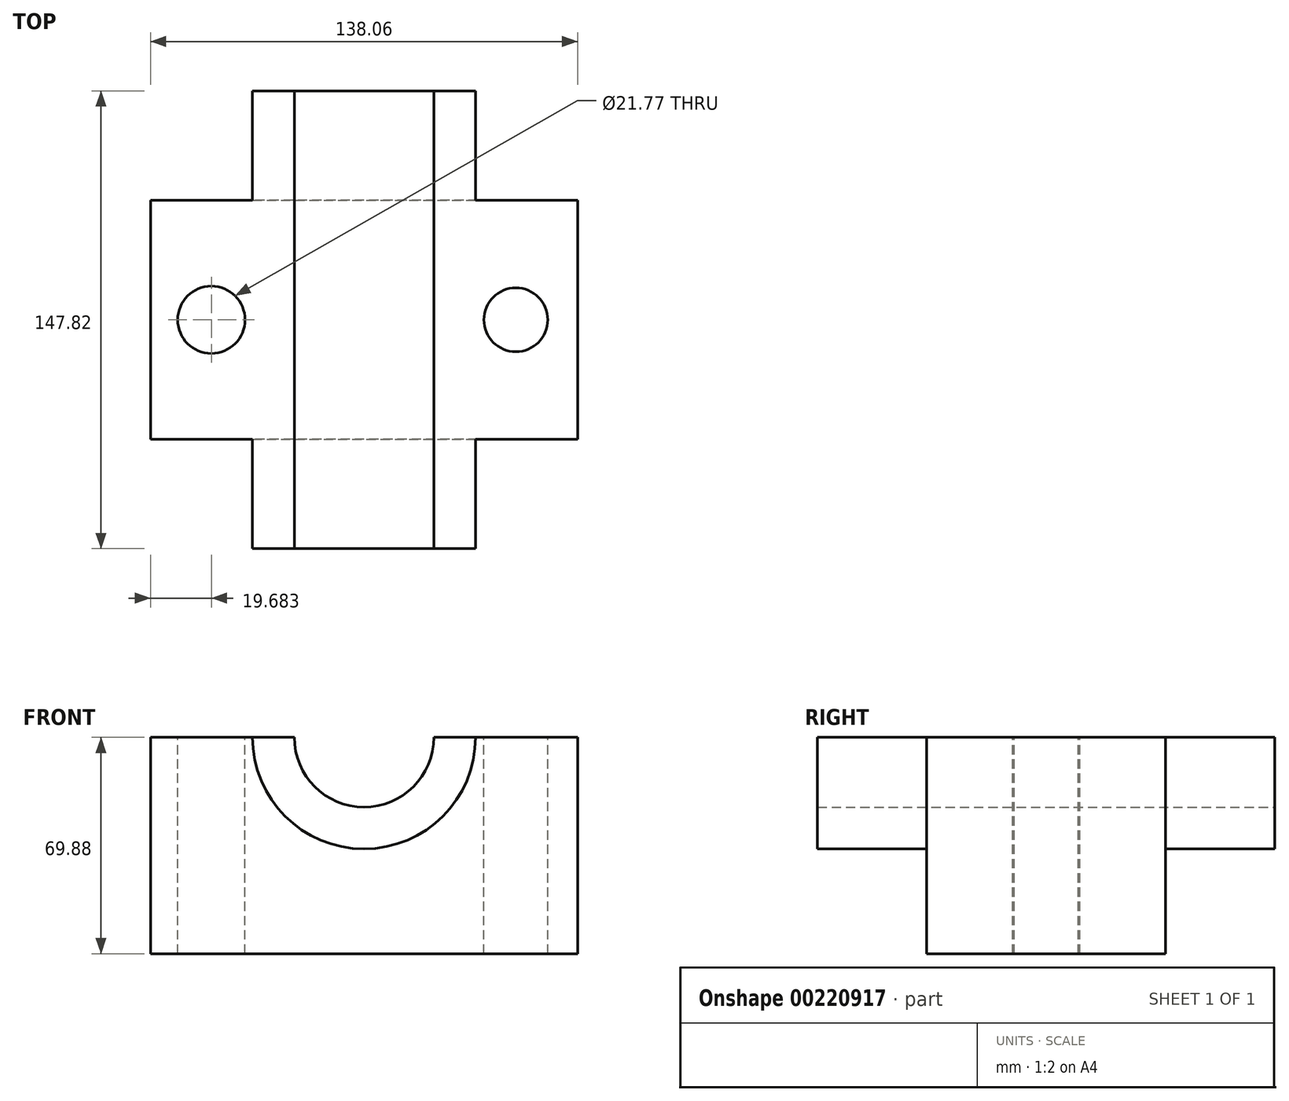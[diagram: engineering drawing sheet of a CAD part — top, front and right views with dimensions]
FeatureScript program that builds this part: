
annotation { "Feature Type Name" : "Feature", "Feature Type Description" : "" }
export const myFeature = defineFeature(function(context is Context, id is Id, definition is map)
    precondition{}
    {
        {
            var Q0;
            Q0=qCreatedBy(makeId("Front.planeOp"),FACE);
            var sketch = newSketch(context, id + "F0", { "sketchPlane" : qUnion([Q0])});
            skLineSegment(sketch, "E0.bottom", {"start": v(69.03, 34.94) * mm, "end": v(-69.03, 34.94) * mm});
            skLineSegment(sketch, "E0.top", {"start": v(69.03, -34.94) * mm, "end": v(-69.03, -34.94) * mm});
            skLineSegment(sketch, "E0.left", {"start": v(69.03, 34.94) * mm, "end": v(69.03, -34.94) * mm});
            skLineSegment(sketch, "E0.right", {"start": v(-69.03, 34.94) * mm, "end": v(-69.03, -34.94) * mm});
            skPoint(sketch, "E0.middle", {"position": v(0, 0) * mm});
            skCircle(sketch, "E1", {"center": v(0, 34.94) * mm, "radius": 36.03 * mm});
            skCircle(sketch, "E2", {"center": v(0, 34.94) * mm, "radius": 22.54 * mm});
            skSolve(sketch);
        }
        {
            var Q0;
            Q0=makeQuery(id+"F0.imprint","IMPRINT",FACE,{"disambiguationData":[TD([[makeQuery(id+"F0.imprint","IMPRINT",EDGE,{"derivedFrom":sQuery(id+"F0.wireOp",EDGE,"E0.bottom")}),1.0]])]});
            extrude(context, id + "F1", {"entities" : qUnion([Q0]), "endBound" : BoundingType.SYMMETRIC, "depth" : 147.83 * mm});
        }
        {
            var Q0;
            Q0 = qSketchRegion(id + "F0", true);
            extrude(context, id + "F2", {"entities" : qUnion([Q0]), "operationType" : NewBodyOperationType.ADD, "endBound" : BoundingType.SYMMETRIC, "oppositeDirection" : true, "depth" : 77.22 * mm});
        }
        {
            var Q0;
            {var subQ0=sQuery(id+"F0.wireOp",EDGE,"E2");var subQ1=sQuery(id+"F0.wireOp",EDGE,"E1");var subQ2=sQuery(id+"F0.wireOp",EDGE,"E0.right");var subQ3=sQuery(id+"F0.wireOp",EDGE,"E0.bottom");var subQ5=sQuery(id+"F0.wireOp",EDGE,"E0.left");var subQ6=makeQuery(id+"F2.opExtrude","CAP_FACE",FACE,{"disambiguationData":[OSD([subQ3,sQuery(id+"F0.wireOp",EDGE,"E0.top"),subQ5,subQ2,subQ1,subQ0])],"isStart":true});Q0=makeQuery(id+"F2.boolean.opBoolean","SPLIT",FACE,{"disambiguationData":[TD([makeQuery(id+"F1.opExtrude","SWEPT_FACE",FACE,{"disambiguationData":[OSD([subQ0])]})])],"derivedFrom":subQ6});}
            extrude(context, id + "F3", {"entities" : qUnion([Q0]), "operationType" : NewBodyOperationType.REMOVE, "oppositeDirection" : true, "depth" : 25.4 * mm});
        }
        {
            var Q0;
            Q0=makeQuery(id+"F3.boolean.opBoolean","COPY",FACE,{"derivedFrom":makeQuery(id+"F3.opExtrude","CAP_FACE",FACE,{"disambiguationData":[OSD([sQuery(id+"F0.wireOp",EDGE,"E0.bottom"),sQuery(id+"F0.wireOp",EDGE,"E0.top"),sQuery(id+"F0.wireOp",EDGE,"E0.left"),sQuery(id+"F0.wireOp",EDGE,"E0.right"),sQuery(id+"F0.wireOp",EDGE,"E1"),sQuery(id+"F0.wireOp",EDGE,"E2")])],"isStart":false})});
            extrude(context, id + "F4", {"entities" : qUnion([Q0]), "operationType" : NewBodyOperationType.REMOVE, "endBound" : BoundingType.THROUGH_ALL, "oppositeDirection" : true, "depth" : 25.4 * mm});
        }
        {
            var Q0;
            {var subQ0=sQuery(id+"F0.wireOp",EDGE,"E2");var subQ1=sQuery(id+"F0.wireOp",EDGE,"E1");var subQ2=sQuery(id+"F0.wireOp",EDGE,"E0.right");var subQ3=sQuery(id+"F0.wireOp",EDGE,"E0.left");var subQ4=sQuery(id+"F0.wireOp",EDGE,"E0.top");var subQ5=sQuery(id+"F0.wireOp",EDGE,"E0.bottom");var subQ6=makeQuery(id+"F2.opExtrude","CAP_FACE",FACE,{"disambiguationData":[OSD([subQ5,subQ4,subQ3,subQ2,subQ1,subQ0])],"isStart":true});var subQ7=makeQuery(id+"F0.imprint","INTERSECT",VERTEX,{"disambiguationData":[OD(1.0)],"derivedFrom":[subQ5,subQ1]});var subQ8=makeQuery(id+"F1.opExtrude","SWEPT_FACE",FACE,{"disambiguationData":[OSD([subQ5]),TDD([makeQuery(id+"F0.imprint","IMPRINT",EDGE,{"disambiguationData":[TD([[subQ7,1.0]])],"derivedFrom":subQ5})])]});var subQ9=makeQuery(id+"F2.boolean.opBoolean","INTERSECT",EDGE,{"derivedFrom":[subQ8,subQ6]});var subQ13=makeQuery(id+"F2.opExtrude","SWEPT_FACE",FACE,{"disambiguationData":[OSD([subQ5]),TDD([makeQuery(id+"F0.imprint","IMPRINT",EDGE,{"disambiguationData":[TD([[makeQuery(id+"F0.imprint","INTERSECT",VERTEX,{"derivedFrom":[subQ5,subQ2]}),1.0]])],"derivedFrom":subQ5})])]});Q0=makeQuery(id+"F4.boolean.opBoolean","MERGE",FACE,{"derivedFrom":[makeQuery(id+"F2.boolean.opBoolean","SPLIT",FACE,{"disambiguationData":[TD([makeQuery(id+"F1.opExtrude","CAP_FACE",FACE,{"disambiguationData":[OSD([subQ5,subQ1,subQ0])],"isStart":true})])],"derivedFrom":subQ8}),makeQuery(id+"F3.boolean.opBoolean","MERGE",FACE,{"derivedFrom":[subQ13,makeQuery(id+"F2.boolean.opBoolean","SPLIT",FACE,{"disambiguationData":[TD([makeQuery(id+"F1.opExtrude","CAP_FACE",FACE,{"disambiguationData":[OSD([subQ5,subQ1,subQ0])],"isStart":false})])],"derivedFrom":subQ8}),makeQuery(id+"F3.opExtrude","SWEPT_FACE",FACE,{"disambiguationData":[OSD([subQ5,subQ4,subQ3,subQ2,subQ1,subQ0]),TDD([subQ9])]})]}),makeQuery(id+"F4.opExtrude","SWEPT_FACE",FACE,{"disambiguationData":[OSD([subQ5,subQ4,subQ3,subQ2,subQ1,subQ0]),TDD([makeQuery(id+"F3.boolean.opBoolean","COPY",EDGE,{"derivedFrom":makeQuery(id+"F3.opExtrude","CAP_EDGE",EDGE,{"disambiguationData":[OSD([subQ5,subQ4,subQ3,subQ2,subQ1,subQ0]),TDD([subQ9])],"isStart":false})})])]})]});}
            var sketch = newSketch(context, id + "F5", { "sketchPlane" : qUnion([Q0])});
            skCircle(sketch, "E3", {"center": v(-49.35, 0) * mm, "radius": 10.89 * mm});
            skCircle(sketch, "E4", {"center": v(49.06, 0) * mm, "radius": 10.32 * mm});
            skSolve(sketch);
        }
        {
            var Q0;
            Q0=makeQuery(id+"F5.imprint","IMPRINT",FACE,{"disambiguationData":[TD([[makeQuery(id+"F5.imprint","IMPRINT",EDGE,{"derivedFrom":sQuery(id+"F5.wireOp",EDGE,"E3")}),1.0]])]});
            var Q1;
            Q1=makeQuery(id+"F5.imprint","IMPRINT",FACE,{"disambiguationData":[TD([[makeQuery(id+"F5.imprint","IMPRINT",EDGE,{"derivedFrom":sQuery(id+"F5.wireOp",EDGE,"E4")}),1.0]])]});
            extrude(context, id + "F6", {"entities" : qUnion([Q0, Q1]), "operationType" : NewBodyOperationType.REMOVE, "endBound" : BoundingType.THROUGH_ALL, "oppositeDirection" : true, "depth" : 25.4 * mm});
        }
    });
